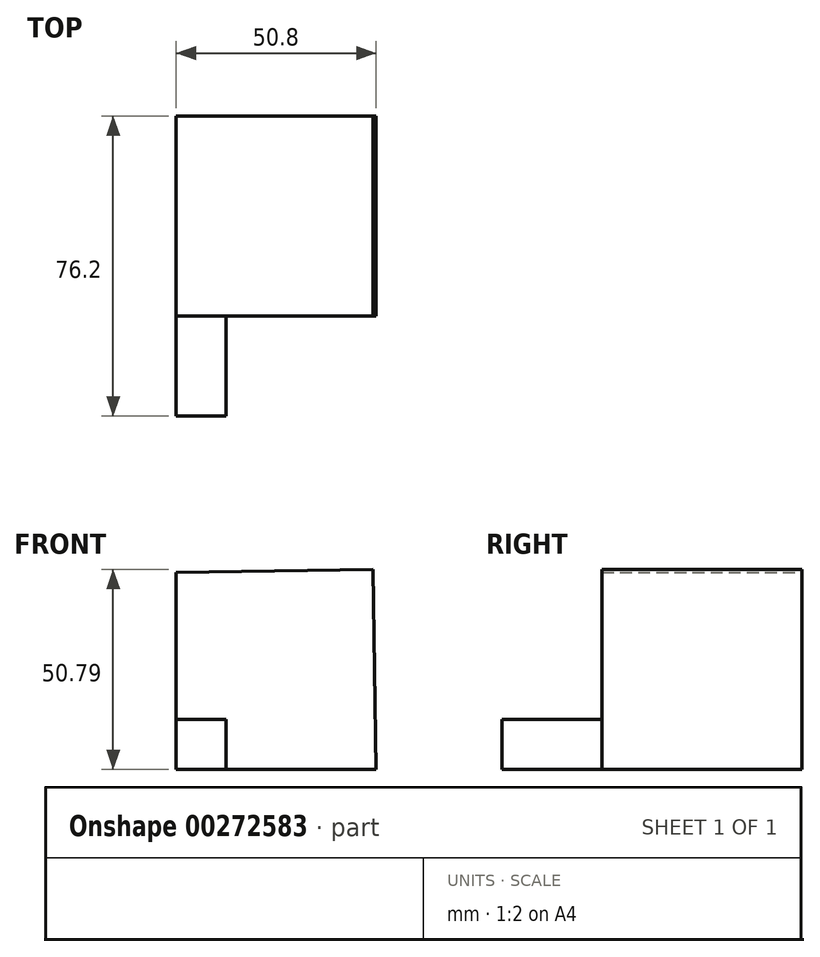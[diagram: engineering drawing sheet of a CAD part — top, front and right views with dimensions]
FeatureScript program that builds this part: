
annotation { "Feature Type Name" : "Feature", "Feature Type Description" : "" }
export const myFeature = defineFeature(function(context is Context, id is Id, definition is map)
    precondition{}
    {
        {
            var Q0;
            Q0=qCreatedBy(makeId("Front.planeOp"),FACE);
            var sketch = newSketch(context, id + "F0", { "sketchPlane" : qUnion([Q0])});
            skLineSegment(sketch, "E0", {"start": v(-50.02, 50.8) * mm, "end": v(-50.02, 0) * mm});
            skLineSegment(sketch, "E1", {"start": v(-50.02, 0) * mm, "end": v(0.78, 0) * mm});
            skLineSegment(sketch, "E2", {"start": v(0.78, 0) * mm, "end": v(0, 50.8) * mm});
            skLineSegment(sketch, "E3", {"start": v(0, 50.8) * mm, "end": v(-50.8, 50) * mm});
            skSolve(sketch);
        }
        {
            var Q0;
            {var subQ0=sQuery(id+"F0.wireOp",EDGE,"E1");Q0=makeQuery(id+"F0.imprint","IMPRINT",FACE,{"disambiguationData":[TD([[makeQuery(id+"F0.imprint","IMPRINT",EDGE,{"derivedFrom":subQ0}),1.0]])]});}
            extrude(context, id + "F1", {"entities" : qUnion([Q0]), "depth" : 50.8 * mm});
        }
        {
            var Q0;
            Q0=makeQuery(id+"F1.opExtrude","CAP_FACE",FACE,{"disambiguationData":[OSD([sQuery(id+"F0.wireOp",EDGE,"E0"),sQuery(id+"F0.wireOp",EDGE,"E1"),sQuery(id+"F0.wireOp",EDGE,"E2"),sQuery(id+"F0.wireOp",EDGE,"E3")])],"isStart":false});
            var sketch = newSketch(context, id + "F2", { "sketchPlane" : qUnion([Q0])});
            skLineSegment(sketch, "E4.bottom", {"start": v(-50.02, 0) * mm, "end": v(-37.32, 0) * mm});
            skLineSegment(sketch, "E4.top", {"start": v(-50.02, 12.7) * mm, "end": v(-37.32, 12.7) * mm});
            skLineSegment(sketch, "E4.left", {"start": v(-50.02, 0) * mm, "end": v(-50.02, 12.7) * mm});
            skLineSegment(sketch, "E4.right", {"start": v(-37.32, 0) * mm, "end": v(-37.32, 12.7) * mm});
            skSolve(sketch);
        }
        {
            var Q0;
            Q0=makeQuery(id+"F2.imprint","IMPRINT",FACE,{"disambiguationData":[TD([[makeQuery(id+"F2.imprint","IMPRINT",EDGE,{"derivedFrom":sQuery(id+"F2.wireOp",EDGE,"E4.bottom")}),1.0]])]});
            extrude(context, id + "F3", {"entities" : qUnion([Q0]), "operationType" : NewBodyOperationType.ADD, "depth" : 25.4 * mm});
        }
    });
